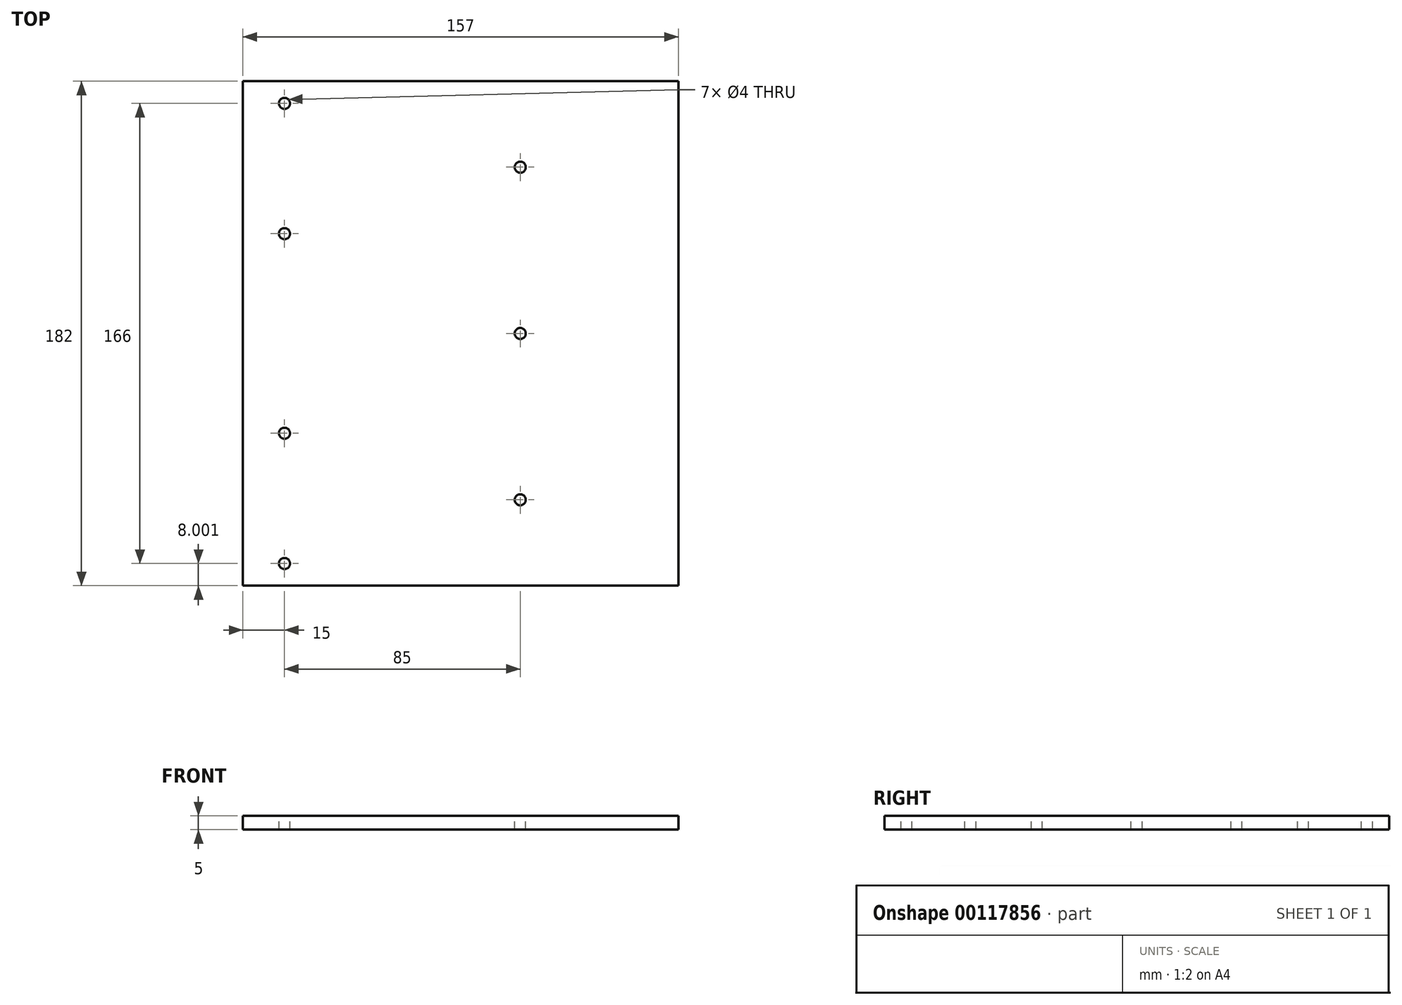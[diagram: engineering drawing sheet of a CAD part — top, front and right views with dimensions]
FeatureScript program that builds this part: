
annotation { "Feature Type Name" : "Feature", "Feature Type Description" : "" }
export const myFeature = defineFeature(function(context is Context, id is Id, definition is map)
    precondition{}
    {
        {
            var Q0;
            Q0=qCreatedBy(makeId("Top.planeOp"),FACE);
            var sketch = newSketch(context, id + "F1", { "sketchPlane" : qUnion([Q0])});
            skLineSegment(sketch, "E0.bottom", {"start": v(0, 36.55) * mm, "end": v(157, 36.55) * mm});
            skLineSegment(sketch, "E0.top", {"start": v(0, 218.55) * mm, "end": v(157, 218.55) * mm});
            skLineSegment(sketch, "E0.left", {"start": v(0, 36.55) * mm, "end": v(0, 218.55) * mm});
            skLineSegment(sketch, "E0.right", {"start": v(157, 36.55) * mm, "end": v(157, 218.55) * mm});
            skSolve(sketch);
        }
        {
            var Q0;
            Q0=makeQuery(id+"F1.imprint","IMPRINT",FACE,{"disambiguationData":[TD([[makeQuery(id+"F1.imprint","IMPRINT",EDGE,{"derivedFrom":sQuery(id+"F1.wireOp",EDGE,"E0.bottom")}),1.0]])]});
            extrude(context, id + "F0", {"entities" : qUnion([Q0]), "depth" : 5 * mm});
        }
        {
            var Q0;
            Q0=makeQuery(id+"F0.opExtrude","CAP_FACE",FACE,{"disambiguationData":[OSD([sQuery(id+"F1.wireOp",EDGE,"E0.bottom"),sQuery(id+"F1.wireOp",EDGE,"E0.top"),sQuery(id+"F1.wireOp",EDGE,"E0.left"),sQuery(id+"F1.wireOp",EDGE,"E0.right")])],"isStart":false});
            var sketch = newSketch(context, id + "F2", { "sketchPlane" : qUnion([Q0])});
            skPoint(sketch, "E1", {"position": v(15, 44.55) * mm});
            skPoint(sketch, "E2", {"position": v(15, 91.55) * mm});
            skPoint(sketch, "E3", {"position": v(100, 127.55) * mm});
            skPoint(sketch, "E4", {"position": v(100, 67.55) * mm});
            skPoint(sketch, "E5", {"position": v(15, 210.55) * mm});
            skPoint(sketch, "E6", {"position": v(15, 163.55) * mm});
            skPoint(sketch, "E7", {"position": v(100, 187.55) * mm});
            skSolve(sketch);
        }
        {
            var Q0;
            Q0=sQuery(id+"F2.wireOp",VERTEX,"E5");
            var Q1;
            Q1=sQuery(id+"F2.wireOp",VERTEX,"E6");
            var Q2;
            Q2=sQuery(id+"F2.wireOp",VERTEX,"E2");
            var Q3;
            Q3=sQuery(id+"F2.wireOp",VERTEX,"E1");
            var Q4;
            Q4=sQuery(id+"F2.wireOp",VERTEX,"E4");
            var Q5;
            Q5=sQuery(id+"F2.wireOp",VERTEX,"E3");
            var Q6;
            Q6=sQuery(id+"F2.wireOp",VERTEX,"E3");
            var Q7;
            Q7=sQuery(id+"F2.wireOp",VERTEX,"E7");
            var Q8;
            Q8=makeQuery(id+"F0.opExtrude","SWEPT_BODY",BODY,{"disambiguationData":[OSD([sQuery(id+"F1.wireOp",EDGE,"E0.bottom"),sQuery(id+"F1.wireOp",EDGE,"E0.top"),sQuery(id+"F1.wireOp",EDGE,"E0.left"),sQuery(id+"F1.wireOp",EDGE,"E0.right")])]});
            hole(context, id + "F3", {"style" : HoleStyle.SIMPLE, "endStyle" : HoleEndStyle.THROUGH, "holeDiameter" : 4 * mm, "locations" : qUnion([Q0, Q1, Q2, Q3, Q4, Q5, Q6, Q7]), "scope" : qUnion([Q8]), "isTappedThrough" : true});
        }
    });
